# Revit family: Zumtobel LF3-A
name_source: partatom
category: Lighting Fixtures
revit_build: Autodesk Revit 2016 (Build: 20150220_1215(x64)
units: mm (PartAtom-declared; Revit-internal decimal feet)

## family parameters
Cut with Voids When Loaded = No
Host = Face
Light Source = Yes
OmniClass Number = 23.80.70.11
OmniClass Title = Luminaries for Internal Lighting
Part Type = Normal
Room Calculation Point = No
Round Connector Dimension = Use Diameter
Shared = No

## types (1)
- LF3 A 4200-940 Q LDE WH
    Apparent Load = 40 VA
    Assembly Code = D5020210
    Body = ZG_Metal_Aluminium
    Color Filter = 16777215
    Cover = ZG_Cover_White_Self_Illumination
    Cover Mini = No
    Default Elevation = 0 mm  [stored 0 ft]
    Description = LED surface-mount luminaire
    Dimming Lamp Color Temperature Shift = <None>
    Emit Shape Visible in Rendering = Yes
    Emit from Rectangle Length = 573 mm  [stored 1.87992 ft]
    Emit from Rectangle Width = 573 mm  [stored 1.87992 ft]
    Height = 51 mm
    Lamp = LED
    Length = 603 mm  [stored 1.97835 ft]
    Manufacturer = Zumtobel Lighting
    Model = 42186940
    Photometric Web File = 42186940_(STD_LEO).IES
    Tilt Angle = -90.00°
    Top Cover Width = 441 mm  [stored 1.44685 ft]
    URL = http://www.zumtobel.com
    Width = 603 mm  [stored 1.97835 ft]

note: [stored X ft] marks values corroborated as IEEE doubles in the binary element streams (Revit-internal decimal feet)

## geometry (parser evidence)
native form markers: Sweep x6
no freeform markers — native parametric forms only
